# Revit family: Auto-Door_Sliding_Single_Wall_Tormax_TX9300FM
name_source: partatom
category: Doors
units: mm (PartAtom-declared; Revit-internal decimal feet)

## family parameters
Always vertical = Yes
Classification Number = 23.30.10.17.11
Cut with Voids When Loaded = No
Host = Wall
Room Calculation Point = No
Shared = No

## types (4) — shared parameters
Analytic Construction = <None>
Assembly Code = B2030110
Available Options = As Noted
Construction Details = http://www.arcat.com
Define Thermal Properties by = Schematic Type
Fire Rating = as Specified
Frame Thickness = 0' - 4 1/2"
Function = Exterior
Glazing Stop Width = 0' - 0 1/4"
Green Building-LEED = http://www.arcat.com
Keynote = 08463
Manufacturer = TORMAX USA Inc.
Manufacturer Fax = 210-494-5930
Manufacturer Website = http://www.tormaxusa.com
Max Height = 0' - 0"
Max Width = 0' - 0"
Miami Dade Conformance = Does Not Apply
Operating Temperature Range = Ambient -30F to 130F
Panel Thickness = 0' - 1 3/4"
Product Data = http://www.arcat.com
Sales Information = http://www.tormaxusa.com
Send Message = http://www.arcat.com
Specification = http://www.arcat.com
Standards Conformance = ANSI A156.10  ;  NFPA 101  ;  UL325  ;  C-UL
Thickness = 0' - 1 3/4"
URL = http://www.tormaxusa.com
Wall Closure = By host
Water Penetration = as Specified
zero-valued in all types: Expected Lifespan (Years), Maintenance Schedule (Months), Warranty Duration (Years)

## per-type parameters (varying)
| type | Description | HD Drive | Model | OX | XO | headerdepth |
| HD Utility Package with Panel by Others OX | Tormax HD Automatic Sliding Door Frame System - TX9300HDFM Utility as Specified with Panel by Others | Yes | TX9300HDFM Utility as Specified | Yes | No | 0' - 7 3/8" |
| HD Utility Package with Panel by Others XO | Tormax HD Automatic Sliding Door Frame System - TX9300HDFM Utility as Specified with Panel by Others | Yes | TX9300HDFM Utility as Specified | No | Yes | 0' - 7 3/8" |
| Utility Package with Panel by Others OX | Tormax Automatic Sliding Door Frame System - TX9300FM Utility as Specified with Panel by Others | No | TX9300FM Utility as Specified | Yes | No | 0' - 6" |
| Utility Package with Panel by Others XO | Tormax Automatic Sliding Door Frame System - TX9300FM Utility as Specified with Panel by Others | No | TX9300FM Utility as Specified | No | Yes | 0' - 6" |

## geometry (parser evidence)
native form markers: Blend x4, Sweep x7
no freeform markers — native parametric forms only
